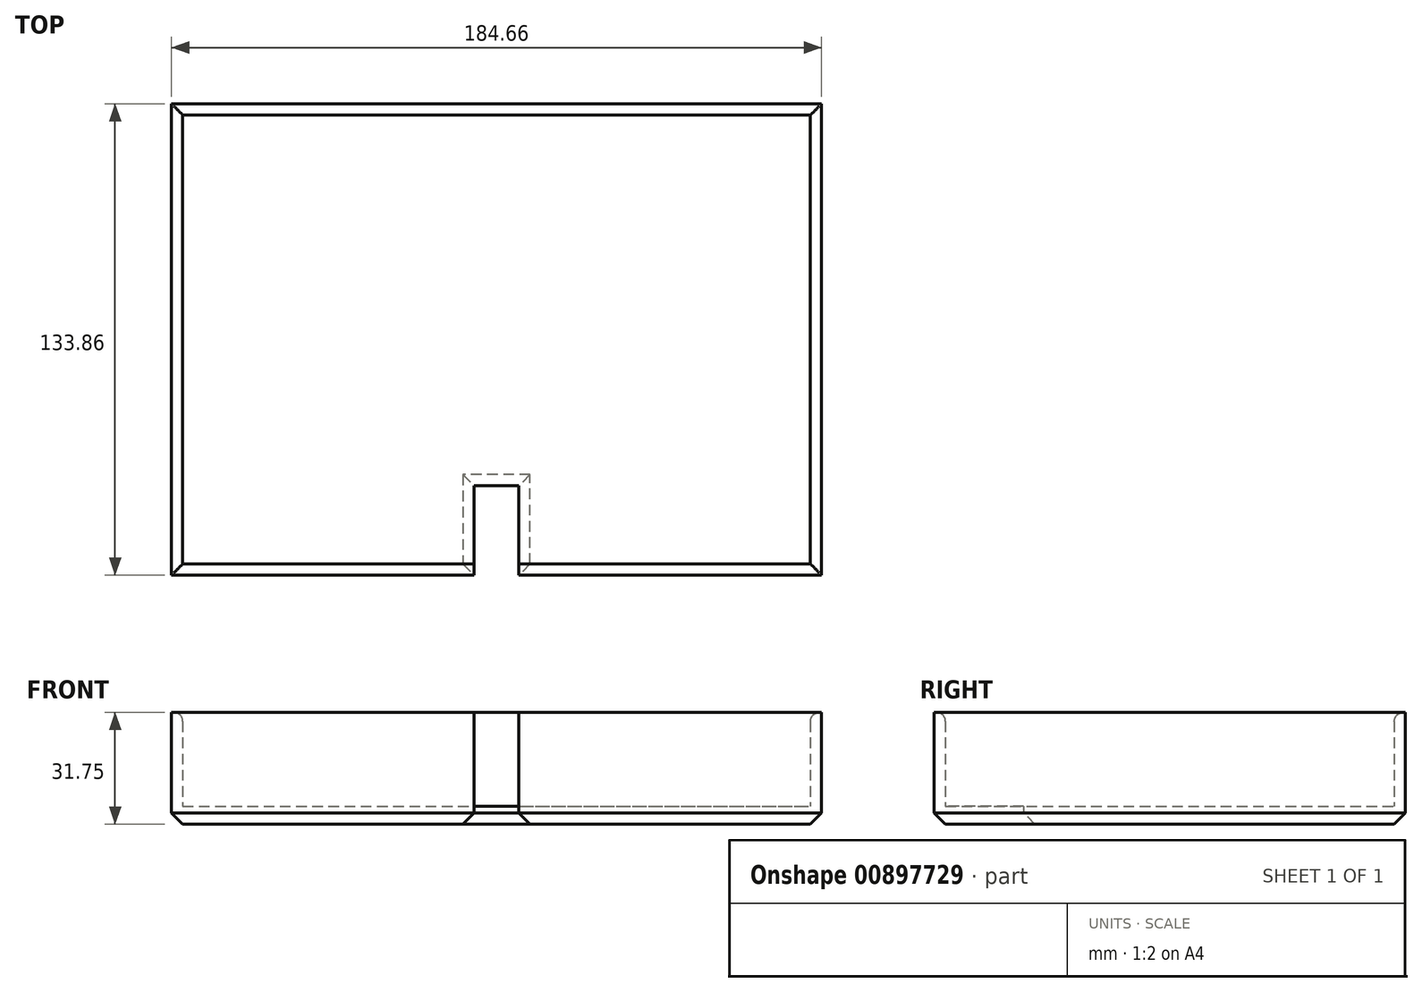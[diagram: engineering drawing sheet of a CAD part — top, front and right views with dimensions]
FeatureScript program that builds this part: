
annotation { "Feature Type Name" : "Feature", "Feature Type Description" : "" }
export const myFeature = defineFeature(function(context is Context, id is Id, definition is map)
    precondition{}
    {
        {
            var Q0;
            Q0=qCreatedBy(makeId("Top.planeOp"),FACE);
            var sketch = newSketch(context, id + "F0", { "sketchPlane" : qUnion([Q0])});
            skLineSegment(sketch, "E0.bottom", {"start": v(92.33, 66.93) * mm, "end": v(-92.33, 66.93) * mm});
            skLineSegment(sketch, "E0.top", {"start": v(92.33, -66.93) * mm, "end": v(-92.33, -66.93) * mm});
            skLineSegment(sketch, "E0.left", {"start": v(92.33, 66.93) * mm, "end": v(92.33, -66.93) * mm});
            skLineSegment(sketch, "E0.right", {"start": v(-92.33, 66.93) * mm, "end": v(-92.33, -66.93) * mm});
            skPoint(sketch, "E0.middle", {"position": v(0, 0) * mm});
            skSolve(sketch);
        }
        {
            var Q0;
            Q0 = qSketchRegion(id + "F0", true);
            extrude(context, id + "F1", {"entities" : qUnion([Q0]), "depth" : 5.08 * mm, "offsetDistance" : 25.4 * mm});
        }
        {
            var Q0;
            Q0=qCreatedBy(makeId("Top.planeOp"),FACE);
            var sketch = newSketch(context, id + "F2", { "sketchPlane" : qUnion([Q0])});
            skLineSegment(sketch, "E1.bottom", {"start": v(92.33, -66.93) * mm, "end": v(-92.33, -66.93) * mm});
            skLineSegment(sketch, "E1.top", {"start": v(92.33, 66.93) * mm, "end": v(-92.33, 66.93) * mm});
            skLineSegment(sketch, "E1.left", {"start": v(92.33, -66.93) * mm, "end": v(92.33, 66.93) * mm});
            skLineSegment(sketch, "E1.right", {"start": v(-92.33, -66.93) * mm, "end": v(-92.33, 66.93) * mm});
            skPoint(sketch, "E1.middle", {"position": v(0, 0) * mm});
            skLineSegment(sketch, "E2.bottom", {"start": v(89.15, 63.75) * mm, "end": v(-89.15, 63.75) * mm});
            skLineSegment(sketch, "E2.top", {"start": v(89.15, -63.75) * mm, "end": v(-89.15, -63.75) * mm});
            skLineSegment(sketch, "E2.left", {"start": v(89.15, 63.75) * mm, "end": v(89.15, -63.75) * mm});
            skLineSegment(sketch, "E2.right", {"start": v(-89.15, 63.75) * mm, "end": v(-89.15, -63.75) * mm});
            skSolve(sketch);
        }
        {
            var Q0;
            Q0 = qSketchRegion(id + "F2", true);
            extrude(context, id + "F3", {"entities" : qUnion([Q0]), "operationType" : NewBodyOperationType.ADD, "depth" : 31.75 * mm, "offsetDistance" : 25.4 * mm});
        }
        {
            var Q0;
            Q0=makeQuery(id+"F3.boolean.opBoolean","MERGE",FACE,{"derivedFrom":[makeQuery(id+"F1.opExtrude","SWEPT_FACE",FACE,{"disambiguationData":[OSD([sQuery(id+"F0.wireOp",EDGE,"E0.top")])]}),makeQuery(id+"F3.opExtrude","SWEPT_FACE",FACE,{"disambiguationData":[OSD([sQuery(id+"F2.wireOp",EDGE,"E1.bottom")])]})]});
            var sketch = newSketch(context, id + "F4", { "sketchPlane" : qUnion([Q0])});
            skLineSegment(sketch, "E3.bottom", {"start": v(6.35, 31.75) * mm, "end": v(-6.35, 31.75) * mm});
            skLineSegment(sketch, "E3.top", {"start": v(6.35, 0) * mm, "end": v(-6.35, 0) * mm});
            skLineSegment(sketch, "E3.left", {"start": v(6.35, 31.75) * mm, "end": v(6.35, 0) * mm});
            skLineSegment(sketch, "E3.right", {"start": v(-6.35, 31.75) * mm, "end": v(-6.35, 0) * mm});
            skPoint(sketch, "E3.middle", {"position": v(0, 15.88) * mm});
            skSolve(sketch);
        }
        {
            var Q0;
            Q0 = qSketchRegion(id + "F4", true);
            extrude(context, id + "F5", {"entities" : qUnion([Q0]), "operationType" : NewBodyOperationType.REMOVE, "oppositeDirection" : true, "depth" : 25.4 * mm, "offsetDistance" : 25.4 * mm});
        }
        {
            var Q0;
            Q0=makeQuery(id+"F1.opExtrude","CAP_FACE",FACE,{"disambiguationData":[OSD([sQuery(id+"F0.wireOp",EDGE,"E0.bottom"),sQuery(id+"F0.wireOp",EDGE,"E0.top"),sQuery(id+"F0.wireOp",EDGE,"E0.left"),sQuery(id+"F0.wireOp",EDGE,"E0.right")])],"isStart":true});
            chamfer(context, id + "F6", {"entities" : qUnion([Q0]), "chamferType" : ChamferType.OFFSET_ANGLE, "width" : 3.17 * mm, "oppositeDirection" : false, "angle" : 45 * degree, "tangentPropagation" : true});
        }
        {
            var Q0;
            {var subQ0=sQuery(id+"F2.wireOp",EDGE,"E2.right");var subQ1=sQuery(id+"F2.wireOp",EDGE,"E2.top");Q0=makeQuery(id+"F5.boolean.opBoolean","SPLIT",EDGE,{"disambiguationData":[TD([makeQuery(id+"F3.opExtrude","SWEPT_FACE",FACE,{"disambiguationData":[OSD([subQ0])]})])],"derivedFrom":makeQuery(id+"F3.opExtrude","CAP_EDGE",EDGE,{"disambiguationData":[OSD([subQ1])],"isStart":false})});}
            var Q1;
            {var subQ0=sQuery(id+"F2.wireOp",EDGE,"E2.left");var subQ1=sQuery(id+"F2.wireOp",EDGE,"E2.top");Q1=makeQuery(id+"F5.boolean.opBoolean","SPLIT",EDGE,{"disambiguationData":[TD([makeQuery(id+"F3.opExtrude","SWEPT_FACE",FACE,{"disambiguationData":[OSD([subQ0])]})])],"derivedFrom":makeQuery(id+"F3.opExtrude","CAP_EDGE",EDGE,{"disambiguationData":[OSD([subQ1])],"isStart":false})});}
            var Q2;
            Q2=makeQuery(id+"F3.opExtrude","CAP_EDGE",EDGE,{"disambiguationData":[OSD([sQuery(id+"F2.wireOp",EDGE,"E2.left")])],"isStart":false});
            var Q3;
            Q3=makeQuery(id+"F3.opExtrude","CAP_EDGE",EDGE,{"disambiguationData":[OSD([sQuery(id+"F2.wireOp",EDGE,"E2.right")])],"isStart":false});
            var Q4;
            Q4=makeQuery(id+"F3.opExtrude","CAP_EDGE",EDGE,{"disambiguationData":[OSD([sQuery(id+"F2.wireOp",EDGE,"E2.bottom")])],"isStart":false});
            fillet(context, id + "F7", {"entities" : qUnion([Q0, Q1, Q2, Q3, Q4]), "radius" : 2.54 * mm, "tangentPropagation" : true, "allowEdgeOverflow" : false});
        }
    });
